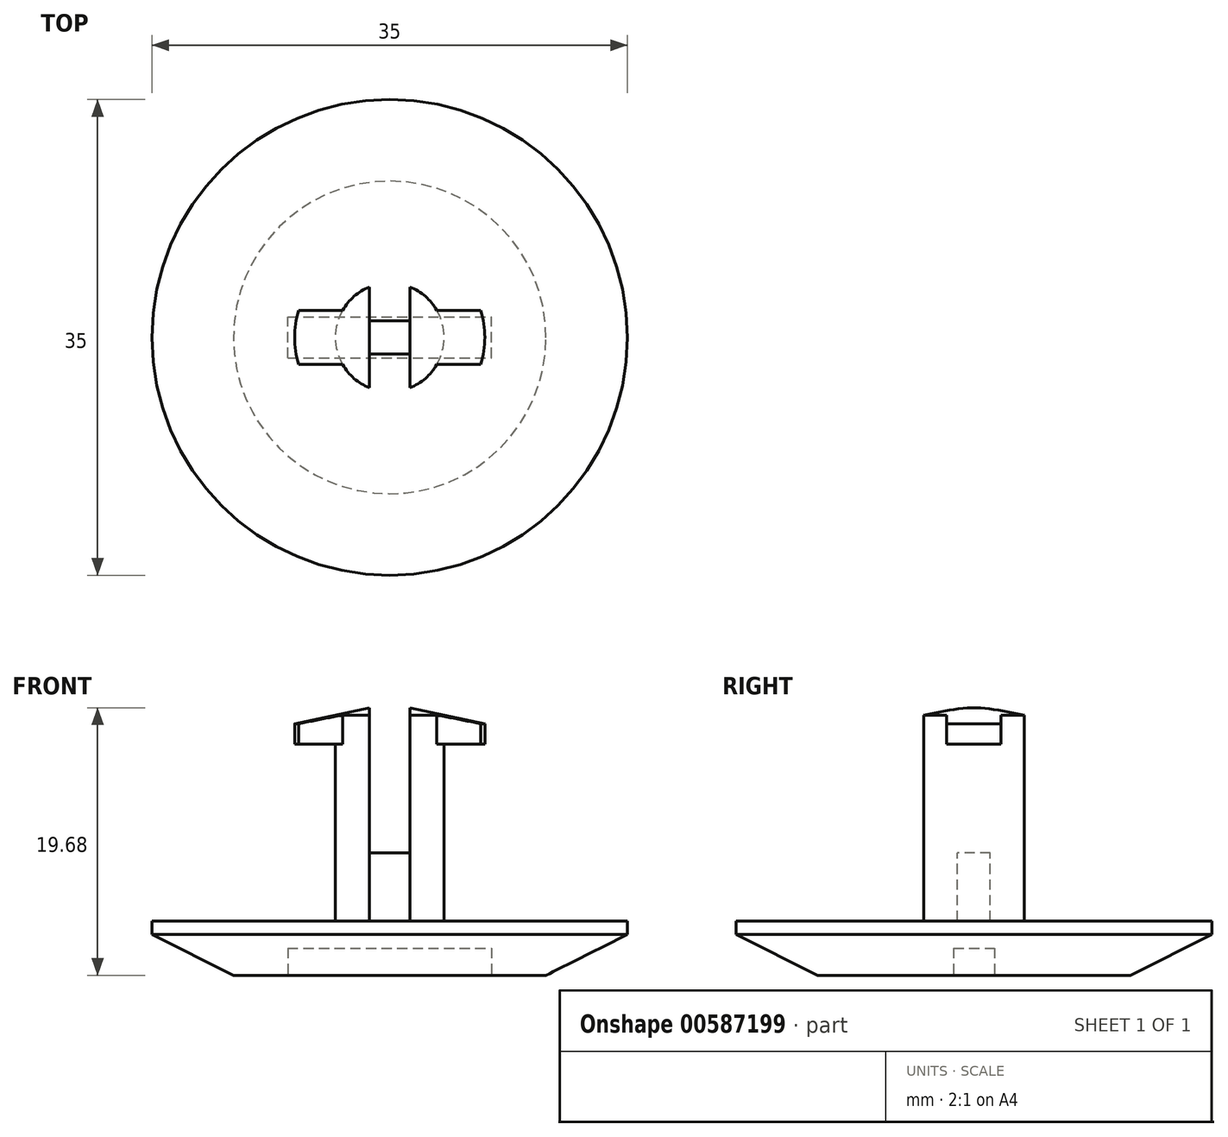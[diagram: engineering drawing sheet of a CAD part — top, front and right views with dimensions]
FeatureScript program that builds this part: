
annotation { "Feature Type Name" : "Feature", "Feature Type Description" : "" }
export const myFeature = defineFeature(function(context is Context, id is Id, definition is map)
    precondition{}
    {
        {
            var Q0;
            Q0=qCreatedBy(makeId("Front.planeOp"),FACE);
            var sketch = newSketch(context, id + "F0", { "sketchPlane" : qUnion([Q0])});
            skLineSegment(sketch, "E0", {"start": v(0, 0) * mm, "end": v(11.5, 0) * mm});
            skLineSegment(sketch, "E1", {"start": v(17.5, 4) * mm, "end": v(4, 4) * mm});
            skLineSegment(sketch, "E2", {"start": v(4, 4) * mm, "end": v(4, 17) * mm});
            skLineSegment(sketch, "E3", {"start": v(4, 17) * mm, "end": v(7, 17) * mm});
            skLineSegment(sketch, "E4", {"start": v(7, 17) * mm, "end": v(7, 18.5) * mm});
            skLineSegment(sketch, "E5", {"start": v(7, 18.5) * mm, "end": v(0, 20) * mm});
            skLineSegment(sketch, "E6", {"start": v(0, 20) * mm, "end": v(0, 0) * mm});
            skLineSegment(sketch, "E7", {"start": v(17.5, 4) * mm, "end": v(17.5, 3) * mm});
            skLineSegment(sketch, "E8", {"start": v(17.5, 3) * mm, "end": v(11.5, 0) * mm});
            skSolve(sketch);
        }
        {
            var Q0;
            Q0=makeQuery(id+"F0.imprint","IMPRINT",FACE,{"disambiguationData":[TD([[makeQuery(id+"F0.imprint","IMPRINT",EDGE,{"derivedFrom":sQuery(id+"F0.wireOp",EDGE,"E0")}),1.0]])]});
            var Q1;
            Q1=sQuery(id+"F0.wireOp",EDGE,"E6");
            revolve(context, id + "F1", {"entities" : qUnion([Q0]), "axis" : qUnion([Q1]), "revolveType" : RevolveType.FULL});
        }
        {
            var Q0;
            Q0=qCreatedBy(makeId("Front.planeOp"),FACE);
            var sketch = newSketch(context, id + "F2", { "sketchPlane" : qUnion([Q0])});
            skLineSegment(sketch, "E9.bottom", {"start": v(-1.5, 20.5) * mm, "end": v(1.5, 20.5) * mm});
            skLineSegment(sketch, "E9.top", {"start": v(-1.5, 9) * mm, "end": v(1.5, 9) * mm});
            skLineSegment(sketch, "E9.left", {"start": v(-1.5, 20.5) * mm, "end": v(-1.5, 9) * mm});
            skLineSegment(sketch, "E9.right", {"start": v(1.5, 20.5) * mm, "end": v(1.5, 9) * mm});
            skSolve(sketch);
        }
        {
            var Q0;
            Q0=makeQuery(id+"F2.imprint","IMPRINT",FACE,{"disambiguationData":[TD([[makeQuery(id+"F2.imprint","IMPRINT",EDGE,{"derivedFrom":sQuery(id+"F2.wireOp",EDGE,"E9.bottom")}),-1.0]])]});
            extrude(context, id + "F3", {"entities" : qUnion([Q0]), "operationType" : NewBodyOperationType.REMOVE, "endBound" : BoundingType.SYMMETRIC, "oppositeDirection" : true, "depth" : 50 * mm, "offsetDistance" : 25 * mm});
        }
        {
            var Q0;
            Q0=makeQuery(id+"F1.opRevolve","SWEPT_FACE",FACE,{"disambiguationData":[OSD([sQuery(id+"F0.wireOp",EDGE,"E1")])]});
            var sketch = newSketch(context, id + "F4", { "sketchPlane" : qUnion([Q0])});
            skLineSegment(sketch, "E10", {"start": v(-3.46, -2) * mm, "end": v(-11.43, -2) * mm});
            skLineSegment(sketch, "E11", {"start": v(-11.43, -2) * mm, "end": v(-11.43, -9.84) * mm});
            skLineSegment(sketch, "E12", {"start": v(-11.43, -9.84) * mm, "end": v(10.35, -9.84) * mm});
            skLineSegment(sketch, "E13", {"start": v(10.35, -9.84) * mm, "end": v(10.35, -2) * mm});
            skLineSegment(sketch, "E14", {"start": v(10.35, -2) * mm, "end": v(3.46, -2) * mm});
            skArc(sketch, "E15", {"start": v(-3.46, -2) * mm, "mid": v(0, -4) * mm, "end": v(3.46, -2) * mm});
            skLineSegment(sketch, "E16", {"start": v(-11.43, 2) * mm, "end": v(-3.46, 2) * mm});
            skLineSegment(sketch, "E17", {"start": v(-11.43, 2) * mm, "end": v(-11.43, 9.08) * mm});
            skLineSegment(sketch, "E18", {"start": v(-11.43, 9.08) * mm, "end": v(10.35, 9.08) * mm});
            skLineSegment(sketch, "E19", {"start": v(10.35, 9.08) * mm, "end": v(10.35, 2) * mm});
            skLineSegment(sketch, "E20", {"start": v(10.35, 2) * mm, "end": v(3.46, 2) * mm});
            skArc(sketch, "E21", {"start": v(3.46, 2) * mm, "mid": v(0, 4) * mm, "end": v(-3.46, 2) * mm});
            skSolve(sketch);
        }
        {
            var Q0;
            Q0 = qSketchRegion(id + "F4", true);
            extrude(context, id + "F5", {"entities" : qUnion([Q0]), "operationType" : NewBodyOperationType.REMOVE, "endBound" : BoundingType.THROUGH_ALL, "depth" : 25 * mm, "offsetDistance" : 25 * mm});
        }
        {
            var Q0;
            Q0=makeQuery(id+"F1.opRevolve","SWEPT_FACE",FACE,{"disambiguationData":[OSD([sQuery(id+"F0.wireOp",EDGE,"E0")])]});
            var sketch = newSketch(context, id + "F6", { "sketchPlane" : qUnion([Q0])});
            skLineSegment(sketch, "E22.bottom", {"start": v(-7.5, 1.5) * mm, "end": v(7.5, 1.5) * mm});
            skLineSegment(sketch, "E22.top", {"start": v(-7.5, -1.5) * mm, "end": v(7.5, -1.5) * mm});
            skLineSegment(sketch, "E22.left", {"start": v(-7.5, 1.5) * mm, "end": v(-7.5, -1.5) * mm});
            skLineSegment(sketch, "E22.right", {"start": v(7.5, 1.5) * mm, "end": v(7.5, -1.5) * mm});
            skSolve(sketch);
        }
        {
            var Q0;
            Q0 = qSketchRegion(id + "F6", true);
            extrude(context, id + "F7", {"entities" : qUnion([Q0]), "operationType" : NewBodyOperationType.REMOVE, "oppositeDirection" : true, "depth" : 2 * mm, "offsetDistance" : 25 * mm});
        }
        {
            var Q0;
            Q0=makeQuery(id+"F3.boolean.opBoolean","COPY",FACE,{"derivedFrom":makeQuery(id+"F3.opExtrude","SWEPT_FACE",FACE,{"disambiguationData":[OSD([sQuery(id+"F2.wireOp",EDGE,"E9.top")])]})});
            var sketch = newSketch(context, id + "F8", { "sketchPlane" : qUnion([Q0])});
            skLineSegment(sketch, "E23.bottom", {"start": v(1.5, 1.2) * mm, "end": v(-1.5, 1.2) * mm});
            skLineSegment(sketch, "E23.top", {"start": v(1.5, 5) * mm, "end": v(-1.5, 5) * mm});
            skLineSegment(sketch, "E23.left", {"start": v(1.5, 1.2) * mm, "end": v(1.5, 5) * mm});
            skLineSegment(sketch, "E23.right", {"start": v(-1.5, 1.2) * mm, "end": v(-1.5, 5) * mm});
            skLineSegment(sketch, "E24.bottom", {"start": v(-1.5, -1.2) * mm, "end": v(1.5, -1.2) * mm});
            skLineSegment(sketch, "E24.top", {"start": v(-1.5, -5) * mm, "end": v(1.5, -5) * mm});
            skLineSegment(sketch, "E24.left", {"start": v(-1.5, -1.2) * mm, "end": v(-1.5, -5) * mm});
            skLineSegment(sketch, "E24.right", {"start": v(1.5, -1.2) * mm, "end": v(1.5, -5) * mm});
            skSolve(sketch);
        }
        {
            var Q0;
            Q0 = qSketchRegion(id + "F8", true);
            var Q1;
            Q1=makeQuery(id+"F1.opRevolve","SWEPT_FACE",FACE,{"disambiguationData":[OSD([sQuery(id+"F0.wireOp",EDGE,"E1")])]});
            extrude(context, id + "F9", {"entities" : qUnion([Q0]), "operationType" : NewBodyOperationType.REMOVE, "endBound" : BoundingType.UP_TO_SURFACE, "oppositeDirection" : true, "depth" : 25 * mm, "endBoundEntityFace" : qUnion([Q1]), "offsetDistance" : 25 * mm});
        }
    });
